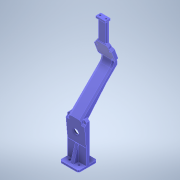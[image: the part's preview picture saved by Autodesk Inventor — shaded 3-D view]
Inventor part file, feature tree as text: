
AUTODESK INVENTOR PART (.ipt)
format: ipt  version: 2022.6 (Build 266554000, 554)  size: 447,488 bytes
history: native  units: mm
features: sketch x11, projected_geometry x6, extrude x5, hole x4, chamfer x3, fillet x2, rib x2, other x1
ambient origin geometry x8: Origin, YZ Plane, XZ Plane, XY Plane, X Axis, Y Axis, Z Axis, Center Point
bodies: Body1 (feature_tree)
feature tree (34):
  extrude  "Extrusion8"  Depth=30.0mm
  hole  "Hole5"  [1 undecoded]
  other  "Bend Part2"
  hole  "Hole6"  [1 undecoded]
  extrude  "Extrusion9"  Depth=28.0mm
  extrude  "Extrusion10"  Depth=5.0mm
  extrude  "Cam extra"  Depth=6.6mm
  hole  "Cam holes"  [1 undecoded]
  extrude  "Extrusion12"  Depth=5.0mm
  hole  "Hole9"  [1 undecoded]
  chamfer  "Chamfer4"  Distance=12.217305mm
  fillet  "Fillet1"  Radius=30.0mm
  sketch  "Sketch29"  dims[d234=45.0deg d235=5.0mm]
  rib  "Rib2"
  rib  "Rib3"
  fillet  "Fillet3"  Radius=5.0mm
  chamfer  "Chamfer5"  Distance=21.0mm
  chamfer  "Chamfer6"  Distance=13.0mm
  sketch  "Sketch18"  dims[d200=3.0mm d201=30.0mm]
  sketch  "Sketch19"  dims[d203=5.0mm d204=60.0mm]
  sketch  "Sketch20"  dims[d205=30.0mm d206=0.0mm d207=15.0mm]
  sketch  "Sketch21"  dims[d208=13.5mm]
  projected_geometry  "Projected Loop3"
  sketch  "Sketch23"  dims[d210=3.4mm d211=6.0mm d212=4.0mm d213=2.0mm d214=90.0deg d215=8.0mm d216=20.594885mm d217=28.0mm]
  projected_geometry  "Projected Loop4"
  sketch  "Sketch24"  dims[d218=3.0mm d219=0.872665mm]
  projected_geometry  "Projected Loop5"
  sketch  "Sketch25"  dims[d220=8.6mm d221=6.0mm d222=15.9mm d223=3.2mm d224=90.0deg d225=8.0mm d226=20.594885mm d228=5.0mm]
  sketch  "Sketch26"  dims[d229=5.0mm d230=0.0mm d231=6.6mm]
  projected_geometry  "Projected Loop6"
  sketch  "Sketch27"  dims[d232=6.6mm d233=1.0mm]
  projected_geometry  "Projected Loop7"
  projected_geometry  "Projected Loop8"
  sketch  "Sketch31"  dims[d237=70.0mm d238=20.0mm d239=0.0mm d240=12.217305mm d241=30.0mm d243=5.0mm d244=21.0mm d245=13.0mm d246=2.4mm d247=6.0mm d248=15.9mm d249=3.2mm d250=90.0deg d251=8.0mm d252=20.594885mm d253=28.0mm d254=20.0mm d255=20.0mm d256=0.0mm d259=15.0mm d260=0.0mm d272=2.0mm d273=2.0mm d274=45.0deg d275=10.0mm d277=50.0mm d279=3.141593mm d280=8.0mm d281=1.0mm d282=5.0mm d283=0.0mm d284=0.0mm d285=1.0mm d286=1.0mm d287=1.0mm d288=5.0mm d289=0.0mm d290=0.0mm d291=1.0mm d292=1.0mm d293=2.0mm d294=3.0mm d295=2.0mm d296=4.363323mm d298=4.0mm d299=35.0mm d300=3.0mm d301=8.0mm d302=9.5mm d303=3.4mm d304=7.0mm d305=4.0mm d306=2.0mm d307=90.0deg d308=5.5mm d309=0.0mm d310=2.0mm d311=2.0mm d312=45.0deg d313=0.0mm d71=0.5mm d72=0.872665mm d73=0.5mm d74=0.872665mm]
note: 4 required parameter values undecoded (feature->parameter linkage not recoverable at this tier; creation-order binding heuristic only, values carry confidence <= 0.55)
